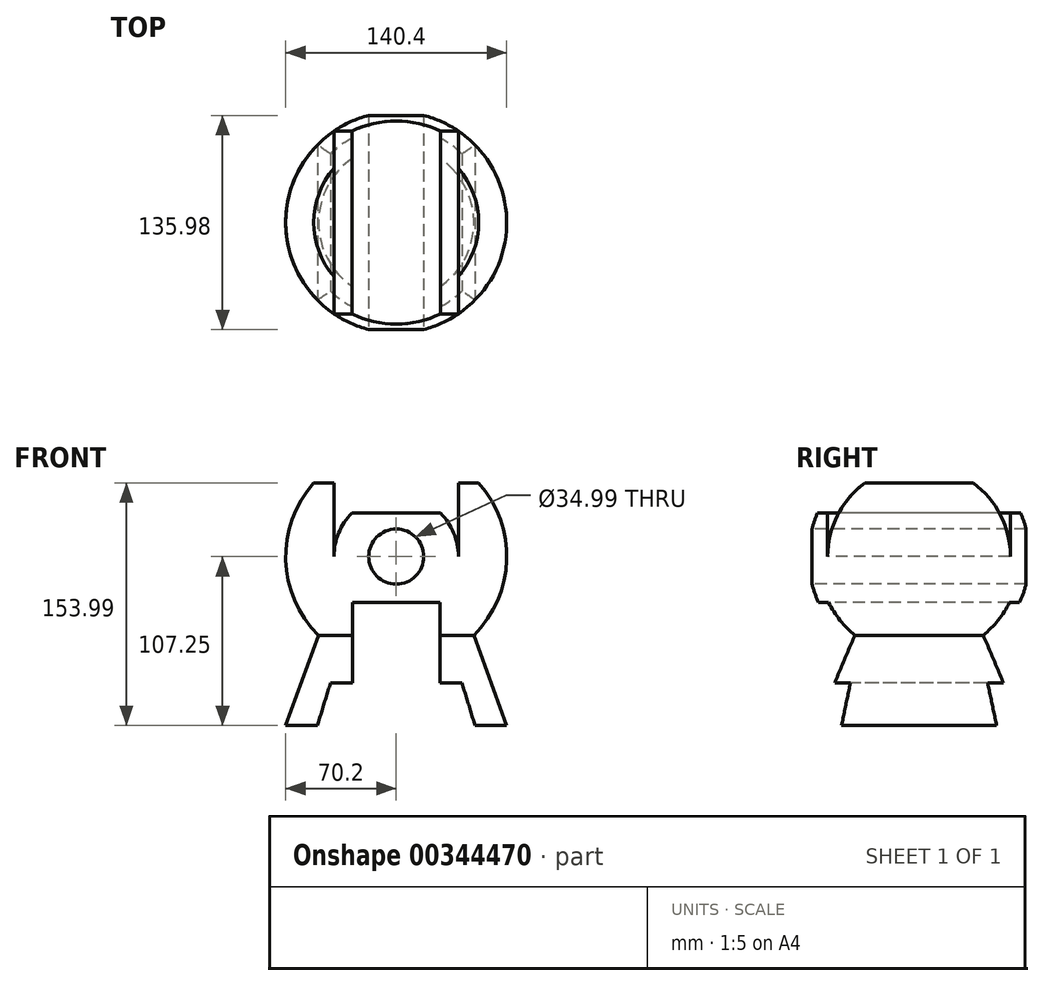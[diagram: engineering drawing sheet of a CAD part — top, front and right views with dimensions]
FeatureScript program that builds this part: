
annotation { "Feature Type Name" : "Feature", "Feature Type Description" : "" }
export const myFeature = defineFeature(function(context is Context, id is Id, definition is map)
    precondition{}
    {
        {
            var Q0;
            Q0=qCreatedBy(makeId("Front.planeOp"),FACE);
            var sketch = newSketch(context, id + "F0", { "sketchPlane" : qUnion([Q0])});
            skArc(sketch, "E0", {"start": v(-52.38, 46.74) * mm, "mid": v(0, -70.2) * mm, "end": v(52.38, 46.74) * mm});
            skLineSegment(sketch, "E1", {"start": v(-52.38, 46.74) * mm, "end": v(52.38, 46.74) * mm});
            skLineSegment(sketch, "E2", {"start": v(0, 0) * mm, "end": v(0, 46.74) * mm});
            skLineSegment(sketch, "E3", {"start": v(-49.33, -49.94) * mm, "end": v(49.33, -49.94) * mm});
            skPoint(sketch, "E4.endSnap0", {"position": v(0, -49.94) * mm});
            skLineSegment(sketch, "E5", {"start": v(0, -71.77) * mm, "end": v(0, 0) * mm});
            skLineSegment(sketch, "E6", {"start": v(70.2, -107.25) * mm, "end": v(70.2, -149.2) * mm});
            skLineSegment(sketch, "E7", {"start": v(70.2, -107.25) * mm, "end": v(70.2, -119.41) * mm});
            skLineSegment(sketch, "E8", {"start": v(70.2, -119.41) * mm, "end": v(70.2, -149.2) * mm});
            skLineSegment(sketch, "E9", {"start": v(41.78, -80.27) * mm, "end": v(0, -80.27) * mm});
            skLineSegment(sketch, "E10", {"start": v(0, -80.27) * mm, "end": v(0, -71.77) * mm});
            skLineSegment(sketch, "E11", {"start": v(49.33, -49.94) * mm, "end": v(70.2, -107.25) * mm});
            skLineSegment(sketch, "E12", {"start": v(70.2, -107.25) * mm, "end": v(52.9, -107.25) * mm});
            skPoint(sketch, "E13.orphan", {"position": v(70.2, 0) * mm});
            skLineSegment(sketch, "E14", {"start": v(41.78, -80.27) * mm, "end": v(62.87, -149.2) * mm});
            skLineSegment(sketch, "E15", {"start": v(62.87, -149.2) * mm, "end": v(70.2, -149.2) * mm});
            skLineSegment(sketch, "E16", {"start": v(52.9, -107.25) * mm, "end": v(50.03, -107.25) * mm});
            skSolve(sketch);
        }
        {
            var Q0;
            {var subQ0=sQuery(id+"F0.wireOp",EDGE,"E2");Q0=makeQuery(id+"F0.imprint","IMPRINT",FACE,{"disambiguationData":[TD([[makeQuery(id+"F0.imprint","IMPRINT",EDGE,{"derivedFrom":subQ0}),-1.0]])]});}
            var Q1;
            {var subQ1=sQuery(id+"F0.wireOp",EDGE,"E0");var subQ3=sQuery(id+"F0.wireOp",EDGE,"E5");var subQ4=makeQuery(id+"F0.imprint","INTERSECT",VERTEX,{"derivedFrom":[subQ1,subQ3]});Q1=makeQuery(id+"F0.imprint","IMPRINT",FACE,{"disambiguationData":[TD([[makeQuery(id+"F0.imprint","IMPRINT",EDGE,{"disambiguationData":[TD([[subQ4,-1.0]])],"derivedFrom":subQ3}),-1.0]])]});}
            var Q2;
            {var subQ0=sQuery(id+"F0.wireOp",EDGE,"E9");Q2=makeQuery(id+"F0.imprint","IMPRINT",FACE,{"disambiguationData":[TD([[makeQuery(id+"F0.imprint","IMPRINT",EDGE,{"derivedFrom":subQ0}),-1.0]])]});}
            var Q3;
            Q3=makeQuery(id+"F0.imprint","IMPRINT",FACE,{"disambiguationData":[TD([[makeQuery(id+"F0.imprint","IMPRINT",EDGE,{"derivedFrom":sQuery(id+"F0.wireOp",EDGE,"E7")}),-1.0]])]});
            var Q4;
            {var subQ0=sQuery(id+"F0.wireOp",EDGE,"E9");Q4=makeQuery(id+"F0.imprint","IMPRINT",FACE,{"disambiguationData":[TD([[makeQuery(id+"F0.imprint","IMPRINT",EDGE,{"derivedFrom":subQ0}),-1.0]])]});}
            var Q5;
            Q5=sQuery(id+"F0.wireOp",EDGE,"E5");
            revolve(context, id + "F1", {"entities" : qUnion([Q0, Q1, Q2, Q3, Q4]), "axis" : qUnion([Q5]), "revolveType" : RevolveType.FULL});
        }
        {
            var Q0;
            Q0=qCreatedBy(makeId("Front.planeOp"),FACE);
            var sketch = newSketch(context, id + "F2", { "sketchPlane" : qUnion([Q0])});
            skCircle(sketch, "E17", {"center": v(0, 0) * mm, "radius": 17.5 * mm});
            skArc(sketch, "E18", {"start": v(-28.15, 27.68) * mm, "mid": v(-36.54, 14.96) * mm, "end": v(-39.48, 0) * mm});
            skLineSegment(sketch, "E19", {"start": v(-28.15, 27.68) * mm, "end": v(28.15, 27.68) * mm});
            skLineSegment(sketch, "E20", {"start": v(0, 0) * mm, "end": v(-17.5, 0) * mm});
            skLineSegment(sketch, "E21", {"start": v(-17.5, 0) * mm, "end": v(-39.48, 0) * mm});
            skLineSegment(sketch, "E22", {"start": v(0, 0) * mm, "end": v(17.5, 0) * mm});
            skLineSegment(sketch, "E23", {"start": v(17.5, 0) * mm, "end": v(39.48, 0) * mm});
            skArc(sketch, "E24.trimOffspring", {"start": v(39.48, 0) * mm, "mid": v(36.54, 14.96) * mm, "end": v(28.15, 27.68) * mm});
            skLineSegment(sketch, "E25", {"start": v(0, 0) * mm, "end": v(0, -167.05) * mm});
            skLineSegment(sketch, "E26", {"start": v(0, -29.15) * mm, "end": v(27.85, -29.15) * mm});
            skLineSegment(sketch, "E27.0", {"start": v(41.78, -80.27) * mm, "end": v(0, -80.27) * mm});
            skLineSegment(sketch, "E28", {"start": v(27.85, -29.15) * mm, "end": v(27.85, -80.27) * mm});
            skLineSegment(sketch, "E29", {"start": v(27.85, -80.27) * mm, "end": v(41.78, -80.27) * mm});
            skLineSegment(sketch, "E30", {"start": v(70.2, -149.2) * mm, "end": v(41.78, -80.27) * mm});
            skLineSegment(sketch, "E31", {"start": v(70.2, -149.2) * mm, "end": v(0, -149.2) * mm});
            skLineSegment(sketch, "E32.MirrorCS", {"start": v(-70.2, -149.2) * mm, "end": v(0, -149.2) * mm});
            skLineSegment(sketch, "E33.MirrorCS", {"start": v(-27.85, -29.15) * mm, "end": v(-27.85, -80.27) * mm});
            skLineSegment(sketch, "E34.MirrorCS", {"start": v(0, -29.15) * mm, "end": v(-27.85, -29.15) * mm});
            skLineSegment(sketch, "E35.MirrorCS", {"start": v(-41.78, -80.27) * mm, "end": v(0, -80.27) * mm});
            skLineSegment(sketch, "E36", {"start": v(39.48, 0) * mm, "end": v(39.48, 52.97) * mm});
            skLineSegment(sketch, "E37", {"start": v(-39.48, 0) * mm, "end": v(-39.48, 52.97) * mm});
            skLineSegment(sketch, "E38", {"start": v(-39.48, 52.97) * mm, "end": v(39.48, 52.97) * mm});
            skLineSegment(sketch, "E39.0", {"start": v(41.78, -80.27) * mm, "end": v(62.87, -149.2) * mm});
            skPoint(sketch, "E40.MirrorCS.end.orphan", {"position": v(-41.78, -80.27) * mm});
            skLineSegment(sketch, "E41.MirrorCS", {"start": v(-41.78, -80.27) * mm, "end": v(-62.87, -149.2) * mm});
            skSolve(sketch);
        }
        {
            var Q0;
            Q0=makeQuery(id+"F2.imprint","IMPRINT",FACE,{"disambiguationData":[TD([[makeQuery(id+"F2.imprint","IMPRINT",EDGE,{"derivedFrom":sQuery(id+"F2.wireOp",EDGE,"E18")}),-1.0]])]});
            var Q1;
            {var subQ0=sQuery(id+"F2.wireOp",EDGE,"E20");Q1=makeQuery(id+"F2.imprint","IMPRINT",FACE,{"disambiguationData":[TD([[makeQuery(id+"F2.imprint","IMPRINT",EDGE,{"derivedFrom":subQ0}),-1.0]])]});}
            var Q2;
            {var subQ0=sQuery(id+"F2.wireOp",EDGE,"E20");Q2=makeQuery(id+"F2.imprint","IMPRINT",FACE,{"disambiguationData":[TD([[makeQuery(id+"F2.imprint","IMPRINT",EDGE,{"derivedFrom":subQ0}),1.0]])]});}
            var Q3;
            {var subQ0=sQuery(id+"F2.wireOp",EDGE,"E22");Q3=makeQuery(id+"F2.imprint","IMPRINT",FACE,{"disambiguationData":[TD([[makeQuery(id+"F2.imprint","IMPRINT",EDGE,{"derivedFrom":subQ0}),-1.0]])]});}
            var Q4;
            {var subQ0=sQuery(id+"F2.wireOp",EDGE,"E27.0");Q4=makeQuery(id+"F2.imprint","IMPRINT",FACE,{"disambiguationData":[TD([[makeQuery(id+"F2.imprint","IMPRINT",EDGE,{"derivedFrom":subQ0}),1.0]])]});}
            var Q5;
            {var subQ5=sQuery(id+"F2.wireOp",EDGE,"E32.MirrorCS");Q5=makeQuery(id+"F2.imprint","IMPRINT",FACE,{"disambiguationData":[TD([[makeQuery(id+"F2.imprint","IMPRINT",EDGE,{"derivedFrom":subQ5}),1.0]])]});}
            var Q6;
            {var subQ4=sQuery(id+"F2.wireOp",EDGE,"E33.MirrorCS");Q6=makeQuery(id+"F2.imprint","IMPRINT",FACE,{"disambiguationData":[TD([[makeQuery(id+"F2.imprint","IMPRINT",EDGE,{"derivedFrom":subQ4}),1.0]])]});}
            var Q7;
            {var subQ0=sQuery(id+"F2.wireOp",EDGE,"E26");Q7=makeQuery(id+"F2.imprint","IMPRINT",FACE,{"disambiguationData":[TD([[makeQuery(id+"F2.imprint","IMPRINT",EDGE,{"derivedFrom":subQ0}),-1.0]])]});}
            extrude(context, id + "F3", {"entities" : qUnion([Q0, Q1, Q2, Q3, Q4, Q5, Q6, Q7]), "operationType" : NewBodyOperationType.REMOVE, "endBound" : BoundingType.SYMMETRIC, "oppositeDirection" : true, "depth" : 295.94 * mm});
        }
    });
